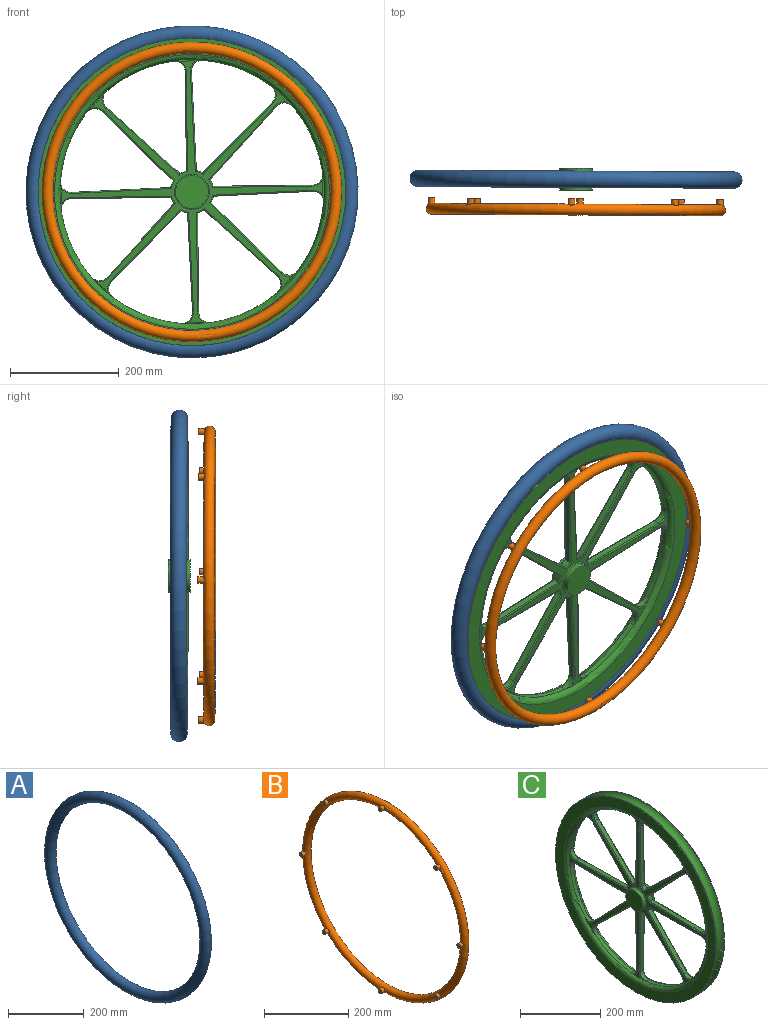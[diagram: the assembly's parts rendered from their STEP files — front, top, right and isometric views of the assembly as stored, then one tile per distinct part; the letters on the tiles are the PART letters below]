
ASSEMBLY  parts=3 mates=2
PART A: 1 faces, bbox 30x660.3x660.3 mm
  f0: torus R=290mm, axis (1,0,0), area 171731.1mm2
PART B: 17 faces, bbox 30x595.3x595.3 mm
  f0: torus R=265mm, axis (1,0,0), area 103668.6mm2, adj f1,f3,f5,f7,f9,f11,f13,f15
  f1: cylinder r=6mm len=12mm, axis (-1,0,0), area 413.7mm2, adj f0,f2
  f2: plane 12x12mm, normal (-1,0,0), area 113.1mm2, adj f1
  f3: cylinder r=6mm len=12mm, axis (-1,0,0), area 413.6mm2, adj f0,f4
  f4: plane 12x12mm, normal (-1,0,0), area 113.1mm2, adj f3
  f5: cylinder r=6mm len=12mm, axis (-1,0,0), area 413.7mm2, adj f0,f6
  f6: plane 12x12mm, normal (-1,0,0), area 113.1mm2, adj f5
  f7: cylinder r=6mm len=12mm, axis (-1,0,0), area 413.7mm2, adj f0,f8
  f8: plane 12x12mm, normal (-1,0,0), area 113.1mm2, adj f7
  f9: cylinder r=6mm len=12mm, axis (-1,0,0), area 413.7mm2, adj f0,f10
  f10: plane 12x12mm, normal (-1,0,0), area 113.1mm2, adj f9
  f11: cylinder r=6mm len=12mm, axis (-1,0,0), area 413.6mm2, adj f0,f12
  f12: plane 12x12mm, normal (-1,0,0), area 113.1mm2, adj f11
  f13: cylinder r=6mm len=12mm, axis (-1,0,0), area 413.7mm2, adj f0,f14
  f14: plane 12x12mm, normal (-1,0,0), area 113.1mm2, adj f13
  f15: cylinder r=6mm len=12mm, axis (-1,0,0), area 413.7mm2, adj f0,f16
  f16: plane 12x12mm, normal (-1,0,0), area 113.1mm2, adj f15
PART C: 175 faces, bbox 40x627.8x627.8 mm
  f0: cylinder r=242.5mm len=122.65mm, axis (-1,0,0), area 1344.7mm2, adj f9,f12,f34,f75
  f1: cylinder r=242.5mm len=122.65mm, axis (-1,0,0), area 1344.7mm2, adj f9,f12,f43,f68
  f2: cylinder r=242.5mm len=122.65mm, axis (-1,0,0), area 1344.7mm2, adj f9,f12,f49,f63
  f3: cylinder r=242.5mm len=122.65mm, axis (-1,0,0), area 1344.7mm2, adj f9,f12,f54,f58
  f4: cylinder r=242.5mm len=122.65mm, axis (-1,0,0), area 1344.7mm2, adj f9,f12,f36,f59
  f5: cylinder r=242.5mm len=122.65mm, axis (-1,0,0), area 1344.7mm2, adj f9,f12,f53,f64
  f6: cylinder r=242.5mm len=122.65mm, axis (-1,0,0), area 1344.7mm2, adj f9,f12,f48,f69
  f7: cylinder r=242.5mm len=122.65mm, axis (-1,0,0), area 1344.7mm2, adj f9,f12,f44,f73
  f8: torus R=290mm, axis (1,0,0), area 54795.1mm2, adj f11,f14
  f9: torus R=252.5mm, axis (1,0,0), area 24292.4mm2, adj f0,f1,f2,f3,f4,f5,f6,f7
  f10: plane 565x565mm, normal (-1,0,0), area 50422.6mm2, adj f9,f11
  f11: cylinder r=282.5mm len=565mm, axis (-1,0,0), area 3567.1mm2, adj f8,f10
  f12: torus R=252.5mm, axis (1,0,0), area 24292.4mm2, adj f0,f1,f2,f3,f4,f5,f6,f7
  f13: plane 565x565mm, normal (1,0,0), area 50422.6mm2, adj f12,f14
  f14: cylinder r=282.5mm len=565mm, axis (-1,0,0), area 3567.1mm2, adj f8,f13
  f15: cylinder r=242.5mm len=55.86mm, axis (-1,0,0), area 28mm2, adj f9,f34,f36,f117
  f16: cylinder r=242.5mm len=55.86mm, axis (-1,0,0), area 28mm2, adj f9,f43,f44,f93
  f17: cylinder r=242.5mm len=55.86mm, axis (-1,0,0), area 28mm2, adj f9,f48,f49,f86
  f18: cylinder r=242.5mm len=55.86mm, axis (-1,0,0), area 28mm2, adj f9,f53,f54,f110
  f19: cylinder r=242.5mm len=39.5mm, axis (-1,0,0), area 28mm2, adj f9,f58,f59,f122
  f20: cylinder r=242.5mm len=39.5mm, axis (-1,0,0), area 28mm2, adj f9,f63,f64,f98
  f21: cylinder r=242.5mm len=39.5mm, axis (-1,0,0), area 28mm2, adj f9,f68,f69,f81
  f22: cylinder r=242.5mm len=39.5mm, axis (-1,0,0), area 28mm2, adj f9,f73,f75,f105
  f23: cylinder r=40mm len=11.77mm, axis (-1,0,0), area 140.7mm2, adj f45,f72,f99,f165
  f24: cylinder r=40mm len=11.77mm, axis (-1,0,0), area 140.7mm2, adj f50,f71,f80,f141
  f25: cylinder r=40mm len=11.77mm, axis (-1,0,0), area 140.7mm2, adj f55,f66,f104,f136
  f26: cylinder r=40mm len=11.77mm, axis (-1,0,0), area 140.7mm2, adj f37,f61,f123,f160
  f27: cylinder r=40mm len=11.77mm, axis (-1,0,0), area 140.7mm2, adj f56,f60,f116,f148
  f28: cylinder r=40mm len=11.77mm, axis (-1,0,0), area 140.7mm2, adj f51,f65,f92,f129
  f29: cylinder r=40mm len=11.77mm, axis (-1,0,0), area 140.7mm2, adj f46,f70,f87,f153
  f30: plane 481x481mm, normal (1,0,0), area 19406.6mm2, adj f126,f127,f128,f129,f130,f131,f132,f133
  f31: plane 481x481mm, normal (-1,0,0), area 19406.6mm2, adj f77,f78,f79,f80,f81,f82,f83,f84
  f32: cylinder r=40mm len=11.77mm, axis (-1,0,0), area 140.7mm2, adj f33,f76,f111,f172
  f33: plane 181.7x11mm, normal (0,0.02,-1), area 1999.1mm2, adj f32,f34,f113,f170
  f34: cylinder r=20mm len=22.3mm, axis (-1,0,0), area 375.3mm2, adj f0,f15,f33,f35,f115,f168
  f35: cylinder r=242.5mm len=55.86mm, axis (-1,0,0), area 28mm2, adj f12,f34,f36,f166
  f36: cylinder r=20mm len=22.3mm, axis (-1,0,0), area 375.3mm2, adj f4,f15,f35,f37,f119,f164
  f37: plane 181.7x11mm, normal (0,0.02,1), area 1999.1mm2, adj f26,f36,f121,f162
  f38: plane 60x60mm, normal (-1,0,0), area 2827.4mm2, adj f39
  f39: cylinder r=30mm len=60mm, axis (-1,0,0), area 1979.2mm2, adj f38,f77
  f40: plane 60x60mm, normal (1,0,0), area 2827.4mm2, adj f41
  f41: cylinder r=30mm len=60mm, axis (-1,0,0), area 1979.2mm2, adj f40,f126
  f42: cylinder r=242.5mm len=55.86mm, axis (-1,0,0), area 28mm2, adj f12,f43,f44,f159
  f43: cylinder r=20mm len=22.3mm, axis (-1,0,0), area 375.3mm2, adj f1,f16,f42,f46,f91,f157
  f44: cylinder r=20mm len=22.3mm, axis (-1,0,0), area 375.3mm2, adj f7,f16,f42,f45,f95,f161
  f45: plane 181.7x11mm, normal (0,1,-0.02), area 1999.1mm2, adj f23,f44,f97,f163
  f46: plane 181.7x11mm, normal (0,-1,-0.02), area 1999.1mm2, adj f29,f43,f89,f155
  f47: cylinder r=242.5mm len=55.86mm, axis (-1,0,0), area 28mm2, adj f12,f48,f49,f135
  f48: cylinder r=20mm len=22.3mm, axis (-1,0,0), area 375.3mm2, adj f6,f17,f47,f50,f84,f137
  f49: cylinder r=20mm len=22.3mm, axis (-1,0,0), area 375.3mm2, adj f2,f17,f47,f51,f88,f133
  f50: plane 181.7x11mm, normal (0,-0.02,-1), area 1999.1mm2, adj f24,f48,f82,f139
  f51: plane 181.7x11mm, normal (0,-0.02,1), area 1999.1mm2, adj f28,f49,f90,f131
  f52: cylinder r=242.5mm len=55.86mm, axis (-1,0,0), area 28mm2, adj f12,f53,f54,f142
  f53: cylinder r=20mm len=22.3mm, axis (-1,0,0), area 375.3mm2, adj f5,f18,f52,f55,f108,f140
  f54: cylinder r=20mm len=22.3mm, axis (-1,0,0), area 375.3mm2, adj f3,f18,f52,f56,f112,f144
  f55: plane 181.7x11mm, normal (0,-1,0.02), area 1999.1mm2, adj f25,f53,f106,f138
  f56: plane 181.7x11mm, normal (0,1,0.02), area 1999.1mm2, adj f27,f54,f114,f146
  f57: cylinder r=242.5mm len=39.5mm, axis (-1,0,0), area 28mm2, adj f12,f58,f59,f154
  f58: cylinder r=20mm len=30.1mm, axis (-1,0,0), area 375.3mm2, adj f3,f19,f57,f60,f120,f152
  f59: cylinder r=20mm len=30.1mm, axis (-1,0,0), area 375.3mm2, adj f4,f19,f57,f61,f124,f156
  f60: plane 131.03x125.94mm, normal (0,-0.69,0.72), area 1999.1mm2, adj f27,f58,f118,f150
  f61: plane 131.03x125.94mm, normal (0,0.72,-0.69), area 1999.1mm2, adj f26,f59,f125,f158
  f62: cylinder r=242.5mm len=39.5mm, axis (-1,0,0), area 28mm2, adj f12,f63,f64,f130
  f63: cylinder r=20mm len=30.1mm, axis (-1,0,0), area 375.3mm2, adj f2,f20,f62,f65,f96,f128
  f64: cylinder r=20mm len=30.1mm, axis (-1,0,0), area 375.3mm2, adj f5,f20,f62,f66,f100,f132
  f65: plane 131.03x125.94mm, normal (0,-0.72,-0.69), area 1999.1mm2, adj f28,f63,f94,f127
  f66: plane 131.03x125.94mm, normal (0,0.69,0.72), area 1999.1mm2, adj f25,f64,f102,f134
  f67: cylinder r=242.5mm len=39.5mm, axis (-1,0,0), area 28mm2, adj f12,f68,f69,f147
  f68: cylinder r=20mm len=30.1mm, axis (-1,0,0), area 375.3mm2, adj f1,f21,f67,f70,f83,f149
  f69: cylinder r=20mm len=30.1mm, axis (-1,0,0), area 375.3mm2, adj f6,f21,f67,f71,f79,f145
  f70: plane 131.03x125.94mm, normal (0,0.69,-0.72), area 1999.1mm2, adj f29,f68,f85,f151
  f71: plane 131.03x125.94mm, normal (0,-0.72,0.69), area 1999.1mm2, adj f24,f69,f78,f143
  f72: plane 131.03x125.94mm, normal (0,-0.69,-0.72), area 1999.1mm2, adj f23,f73,f101,f167
  f73: cylinder r=20mm len=30.1mm, axis (-1,0,0), area 375.3mm2, adj f7,f22,f72,f74,f103,f169
  f74: cylinder r=242.5mm len=39.5mm, axis (-1,0,0), area 28mm2, adj f12,f73,f75,f171
  f75: cylinder r=20mm len=30.1mm, axis (-1,0,0), area 375.3mm2, adj f0,f22,f74,f76,f107,f173
  f76: plane 131.03x125.94mm, normal (0,0.72,0.69), area 1999.1mm2, adj f32,f75,f109,f174
  f77: torus R=32mm, axis (1,0,0), area 606.5mm2, adj f31,f39
  f78: cylinder r=2mm len=133.55mm, axis (0,-0.69,-0.72), area 572.7mm2, adj f31,f71,f79,f80
  f79: torus R=22mm, axis (1,0,0), area 88.4mm2, adj f31,f69,f78,f81
  f80: torus R=38mm, axis (1,0,0), area 43mm2, adj f24,f31,f78,f82
  f81: torus R=240.5mm, axis (1,0,0), area 131.7mm2, adj f21,f31,f79,f83
  f82: cylinder r=2mm len=183.32mm, axis (0,1,-0.02), area 572.7mm2, adj f31,f50,f80,f84
  f83: torus R=22mm, axis (1,0,0), area 88.4mm2, adj f31,f68,f81,f85
  f84: torus R=22mm, axis (1,0,0), area 88.4mm2, adj f31,f48,f82,f86
  f85: cylinder r=2mm len=133.55mm, axis (0,0.72,0.69), area 572.7mm2, adj f31,f70,f83,f87
  f86: torus R=240.5mm, axis (1,0,0), area 131.7mm2, adj f17,f31,f84,f88
  f87: torus R=38mm, axis (1,0,0), area 43mm2, adj f29,f31,f85,f89
  f88: torus R=22mm, axis (1,0,0), area 88.4mm2, adj f31,f49,f86,f90
  f89: cylinder r=2mm len=183.32mm, axis (0,0.02,-1), area 572.7mm2, adj f31,f46,f87,f91
  f90: cylinder r=2mm len=183.32mm, axis (0,-1,-0.02), area 572.7mm2, adj f31,f51,f88,f92
  f91: torus R=22mm, axis (1,0,0), area 88.4mm2, adj f31,f43,f89,f93
  f92: torus R=38mm, axis (1,0,0), area 43mm2, adj f28,f31,f90,f94
  f93: torus R=240.5mm, axis (1,0,0), area 131.7mm2, adj f16,f31,f91,f95
  f94: cylinder r=2mm len=133.55mm, axis (0,0.69,-0.72), area 572.7mm2, adj f31,f65,f92,f96
  f95: torus R=22mm, axis (1,0,0), area 88.4mm2, adj f31,f44,f93,f97
  f96: torus R=22mm, axis (1,0,0), area 88.4mm2, adj f31,f63,f94,f98
  f97: cylinder r=2mm len=183.32mm, axis (0,0.02,1), area 572.7mm2, adj f31,f45,f95,f99
  f98: torus R=240.5mm, axis (1,0,0), area 131.7mm2, adj f20,f31,f96,f100
  f99: torus R=38mm, axis (1,0,0), area 43mm2, adj f23,f31,f97,f101
  f100: torus R=22mm, axis (1,0,0), area 88.4mm2, adj f31,f64,f98,f102
  f101: cylinder r=2mm len=133.55mm, axis (0,0.72,-0.69), area 572.7mm2, adj f31,f72,f99,f103
  f102: cylinder r=2mm len=133.55mm, axis (0,-0.72,0.69), area 572.7mm2, adj f31,f66,f100,f104
  f103: torus R=22mm, axis (1,0,0), area 88.4mm2, adj f31,f73,f101,f105
  f104: torus R=38mm, axis (1,0,0), area 43mm2, adj f25,f31,f102,f106
  f105: torus R=240.5mm, axis (1,0,0), area 131.7mm2, adj f22,f31,f103,f107
  f106: cylinder r=2mm len=183.32mm, axis (0,-0.02,-1), area 572.7mm2, adj f31,f55,f104,f108
  f107: torus R=22mm, axis (1,0,0), area 88.4mm2, adj f31,f75,f105,f109
  f108: torus R=22mm, axis (1,0,0), area 88.4mm2, adj f31,f53,f106,f110
  f109: cylinder r=2mm len=133.55mm, axis (0,-0.69,0.72), area 572.7mm2, adj f31,f76,f107,f111
  f110: torus R=240.5mm, axis (1,0,0), area 131.7mm2, adj f18,f31,f108,f112
  f111: torus R=38mm, axis (1,0,0), area 43mm2, adj f31,f32,f109,f113
  f112: torus R=22mm, axis (1,0,0), area 88.4mm2, adj f31,f54,f110,f114
  f113: cylinder r=2mm len=183.32mm, axis (0,1,0.02), area 572.7mm2, adj f31,f33,f111,f115
  f114: cylinder r=2mm len=183.32mm, axis (0,-0.02,1), area 572.7mm2, adj f31,f56,f112,f116
  f115: torus R=22mm, axis (1,0,0), area 88.4mm2, adj f31,f34,f113,f117
  f116: torus R=38mm, axis (1,0,0), area 43mm2, adj f27,f31,f114,f118
  f117: torus R=240.5mm, axis (1,0,0), area 131.7mm2, adj f15,f31,f115,f119
  f118: cylinder r=2mm len=133.55mm, axis (0,-0.72,-0.69), area 572.7mm2, adj f31,f60,f116,f120
  f119: torus R=22mm, axis (1,0,0), area 88.4mm2, adj f31,f36,f117,f121
  f120: torus R=22mm, axis (1,0,0), area 88.4mm2, adj f31,f58,f118,f122
  f121: cylinder r=2mm len=183.32mm, axis (0,-1,0.02), area 572.7mm2, adj f31,f37,f119,f123
  f122: torus R=240.5mm, axis (1,0,0), area 131.7mm2, adj f19,f31,f120,f124
  f123: torus R=38mm, axis (1,0,0), area 43mm2, adj f26,f31,f121,f125
  f124: torus R=22mm, axis (1,0,0), area 88.4mm2, adj f31,f59,f122,f125
  f125: cylinder r=2mm len=133.55mm, axis (0,0.69,0.72), area 572.7mm2, adj f31,f61,f123,f124
  f126: torus R=32mm, axis (1,0,0), area 606.5mm2, adj f30,f41
  f127: cylinder r=2mm len=133.55mm, axis (0,-0.69,0.72), area 572.7mm2, adj f30,f65,f128,f129
  f128: torus R=22mm, axis (1,0,0), area 88.4mm2, adj f30,f63,f127,f130
  f129: torus R=38mm, axis (1,0,0), area 43mm2, adj f28,f30,f127,f131
  f130: torus R=240.5mm, axis (1,0,0), area 131.7mm2, adj f30,f62,f128,f132
  f131: cylinder r=2mm len=183.32mm, axis (0,1,0.02), area 572.7mm2, adj f30,f51,f129,f133
  f132: torus R=22mm, axis (1,0,0), area 88.4mm2, adj f30,f64,f130,f134
  f133: torus R=22mm, axis (1,0,0), area 88.4mm2, adj f30,f49,f131,f135
  f134: cylinder r=2mm len=133.55mm, axis (0,0.72,-0.69), area 572.7mm2, adj f30,f66,f132,f136
  f135: torus R=240.5mm, axis (1,0,0), area 131.7mm2, adj f30,f47,f133,f137
  f136: torus R=38mm, axis (1,0,0), area 43mm2, adj f25,f30,f134,f138
  f137: torus R=22mm, axis (1,0,0), area 88.4mm2, adj f30,f48,f135,f139
  f138: cylinder r=2mm len=183.32mm, axis (0,0.02,1), area 572.7mm2, adj f30,f55,f136,f140
  f139: cylinder r=2mm len=183.32mm, axis (0,-1,0.02), area 572.7mm2, adj f30,f50,f137,f141
  f140: torus R=22mm, axis (1,0,0), area 88.4mm2, adj f30,f53,f138,f142
  f141: torus R=38mm, axis (1,0,0), area 43mm2, adj f24,f30,f139,f143
  f142: torus R=240.5mm, axis (1,0,0), area 131.7mm2, adj f30,f52,f140,f144
  f143: cylinder r=2mm len=133.55mm, axis (0,0.69,0.72), area 572.7mm2, adj f30,f71,f141,f145
  f144: torus R=22mm, axis (1,0,0), area 88.4mm2, adj f30,f54,f142,f146
  f145: torus R=22mm, axis (1,0,0), area 88.4mm2, adj f30,f69,f143,f147
  f146: cylinder r=2mm len=183.32mm, axis (0,0.02,-1), area 572.7mm2, adj f30,f56,f144,f148
  f147: torus R=240.5mm, axis (1,0,0), area 131.7mm2, adj f30,f67,f145,f149
  f148: torus R=38mm, axis (1,0,0), area 43mm2, adj f27,f30,f146,f150
  f149: torus R=22mm, axis (1,0,0), area 88.4mm2, adj f30,f68,f147,f151
  f150: cylinder r=2mm len=133.55mm, axis (0,0.72,0.69), area 572.7mm2, adj f30,f60,f148,f152
  f151: cylinder r=2mm len=133.55mm, axis (0,-0.72,-0.69), area 572.7mm2, adj f30,f70,f149,f153
  f152: torus R=22mm, axis (1,0,0), area 88.4mm2, adj f30,f58,f150,f154
  f153: torus R=38mm, axis (1,0,0), area 43mm2, adj f29,f30,f151,f155
  f154: torus R=240.5mm, axis (1,0,0), area 131.7mm2, adj f30,f57,f152,f156
  f155: cylinder r=2mm len=183.32mm, axis (0,-0.02,1), area 572.7mm2, adj f30,f46,f153,f157
  f156: torus R=22mm, axis (1,0,0), area 88.4mm2, adj f30,f59,f154,f158
  f157: torus R=22mm, axis (1,0,0), area 88.4mm2, adj f30,f43,f155,f159
  f158: cylinder r=2mm len=133.55mm, axis (0,-0.69,-0.72), area 572.7mm2, adj f30,f61,f156,f160
  f159: torus R=240.5mm, axis (1,0,0), area 131.7mm2, adj f30,f42,f157,f161
  f160: torus R=38mm, axis (1,0,0), area 43mm2, adj f26,f30,f158,f162
  f161: torus R=22mm, axis (1,0,0), area 88.4mm2, adj f30,f44,f159,f163
  f162: cylinder r=2mm len=183.32mm, axis (0,1,-0.02), area 572.7mm2, adj f30,f37,f160,f164
  f163: cylinder r=2mm len=183.32mm, axis (0,-0.02,-1), area 572.7mm2, adj f30,f45,f161,f165
  f164: torus R=22mm, axis (1,0,0), area 88.4mm2, adj f30,f36,f162,f166
  f165: torus R=38mm, axis (1,0,0), area 43mm2, adj f23,f30,f163,f167
  f166: torus R=240.5mm, axis (1,0,0), area 131.7mm2, adj f30,f35,f164,f168
  f167: cylinder r=2mm len=133.55mm, axis (0,-0.72,0.69), area 572.7mm2, adj f30,f72,f165,f169
  f168: torus R=22mm, axis (1,0,0), area 88.4mm2, adj f30,f34,f166,f170
  f169: torus R=22mm, axis (1,0,0), area 88.4mm2, adj f30,f73,f167,f171
  f170: cylinder r=2mm len=183.32mm, axis (0,-1,-0.02), area 572.7mm2, adj f30,f33,f168,f172
  f171: torus R=240.5mm, axis (1,0,0), area 131.7mm2, adj f30,f74,f169,f173
  f172: torus R=38mm, axis (1,0,0), area 43mm2, adj f30,f32,f170,f174
  f173: torus R=22mm, axis (1,0,0), area 88.4mm2, adj f30,f75,f171,f174
  f174: cylinder r=2mm len=133.55mm, axis (0,0.69,-0.72), area 572.7mm2, adj f30,f76,f172,f173
PLACE A rot(axis=(0.58,-0.58,-0.57),121.2deg) t=(-264.44,-366.32,225.06)mm
PLACE B rot(axis=(0.58,-0.58,-0.57),121.2deg) t=(-264.55,-387.01,225.03)mm
PLACE C rot(axis=(0.58,-0.58,-0.57),121.2deg) t=(-264.44,-366.32,225.06)mm
MATE revolute A.f0 <-> C.f0  axis (-0.01,-1,0) through (24.73,-663.28,540.24)mm
MATE cylindrical B.f0 <-> C.f0  axis (-0.01,-1,0) through (24.44,-718.96,540.16)mm
